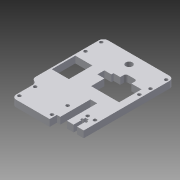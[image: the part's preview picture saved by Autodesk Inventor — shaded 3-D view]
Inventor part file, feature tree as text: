
AUTODESK INVENTOR PART (.ipt)
format: ipt  version: 2013 (Build 170138000, 138)  size: 148,480 bytes
history: native  units: mm
features: extrude x1, sketch x1
ambient origin geometry x8: Origin, YZ Plane, XZ Plane, XY Plane, X Axis, Y Axis, Z Axis, Center Point
bodies: Solid1 (feature_tree)
feature tree (2):
  extrude  "Extrusion1"  [1 undecoded]
  sketch  "Sketch1"  dims[d0=6.0mm d1=0.0mm]
note: 1 required parameter value undecoded (feature->parameter linkage not recoverable at this tier; creation-order binding heuristic only, values carry confidence <= 0.55)
